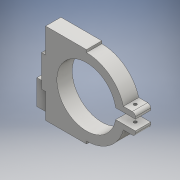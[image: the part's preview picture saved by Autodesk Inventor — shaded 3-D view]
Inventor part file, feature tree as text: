
AUTODESK INVENTOR PART (.ipt)
format: ipt  version: 2016 (Build 200138000, 138)  size: 178,688 bytes
history: native  units: mm
features: sketch x8, extrude x6, hole x2, fillet x1
ambient origin geometry x8: Origin, YZ Plane, XZ Plane, XY Plane, X Axis, Y Axis, Z Axis, Center Point
bodies: Solid1 (feature_tree)
feature tree (17):
  extrude  "Extrusion1"  Depth=80.0mm
  hole  "Hole1"  [1 undecoded]
  extrude  "Extrusion2"  Depth=10.0mm
  extrude  "Extrusion3"  Depth=15.0mm
  extrude  "Extrusion4"  Depth=15.0mm TaperAngle=0.0deg
  fillet  "Fillet1"  Radius=3.0mm
  hole  "Hole2"  [1 undecoded]
  extrude  "Extrusion5"  Depth=24.5mm
  extrude  "Extrusion6"  Depth=4.0mm TaperAngle=0.0deg
  sketch  "Sketch1"  dims[d0=80.0mm d1=80.0mm]
  sketch  "Sketch2"  dims[d2=15.0mm d3=0.0mm]
  sketch  "Sketch3"  dims[d4=58.0mm d5=6.0mm d6=4.0mm d7=2.0mm d8=90.0deg d9=8.0mm d10=20.594885mm d11=75.0mm]
  sketch  "Sketch4"  dims[d12=15.0mm d13=0.0mm d14=10.0mm]
  sketch  "Sketch5"  dims[d15=15.0mm d16=0.0mm d17=15.0mm]
  sketch  "Sketch6"  dims[d18=5.0mm d19=15.0mm d20=0.0mm d21=3.0mm]
  sketch  "Sketch7"  dims[d22=4.6155mm]
  sketch  "Sketch8"  dims[d23=3.0mm d24=6.0mm d25=4.0mm d26=2.0mm d27=90.0deg d28=8.0mm d29=20.594885mm d30=31.0mm d31=24.5mm d32=4.0mm d33=0.0mm d34=7.5mm d35=16.0mm d36=0.0mm]
note: 2 required parameter values undecoded (feature->parameter linkage not recoverable at this tier; creation-order binding heuristic only, values carry confidence <= 0.55)
